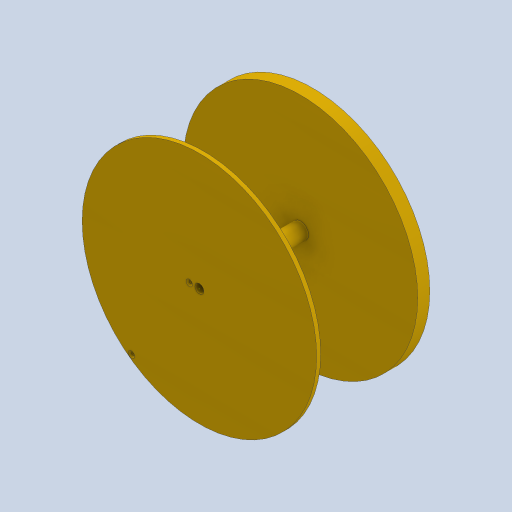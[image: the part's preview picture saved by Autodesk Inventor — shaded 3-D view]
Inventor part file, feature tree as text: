
AUTODESK INVENTOR PART (.ipt)
format: ipt  version: 2024 (Build 280153000, 153)  size: 301,056 bytes
history: native  units: in
note: dims shown in document units (in); Inventor stores cm internally (conversion verified against a paired STEP export)
features: extrude x5, other x2, sketch x1, chamfer x1, hole x1, loft x1
ambient origin geometry x8: Origin, YZ Plane, XZ Plane, XY Plane, X Axis, Y Axis, Z Axis, Center Point
bodies: Solid1 (feature_tree), Solid2 (feature_tree)
feature tree (11):
  extrude  "Extrusion1"  Depth=0.1181in TaperAngle=0.0deg
  extrude  "Extrusion2"  Depth=0.1102in
  extrude  "Extrusion3"  Depth=0.9449in TaperAngle=0.0deg
  extrude  "Extrusion4"  Depth=0.1102in
  sketch  "Sketch6"  dims[d0=2.2835in d1=0.1181in d2=0.0in d3=0.1575in d4=0.9449in d5=0.0in d6=2.2835in d7=0.0394in d8=0.0in d9=0.0866in d10=0.2028in d11=0.0in d20=0.0315in d21=0.0315in d22=0.0591in d23=0.0in d24=0.0157in d25=0.0787in d26=45.0deg d32=0.0984in d34=0.0968in d35=0.2362in d36=0.1575in d37=0.0787in d38=90.0deg d39=0.1102in d40=0.0in d41=0.8858in d44=0.4331in d45=0.4331in d46=0.4528in d47=0.4528in d48=0.1969in d49=0.1969in d50=0.0in d51=90.0deg d52=0.0in d53=90.0deg]
  extrude  "Extrusion5"  Depth=0.0394in TaperAngle=0.0deg
  chamfer  "Chamfer1"  Distance=0.0866in
  hole  "Hole2"  [1 undecoded]
  loft  "Loft1"
  other  "Edges1"
  other  "Edges2"
note: 1 required parameter value undecoded (feature->parameter linkage not recoverable at this tier; creation-order binding heuristic only, values carry confidence <= 0.55)
